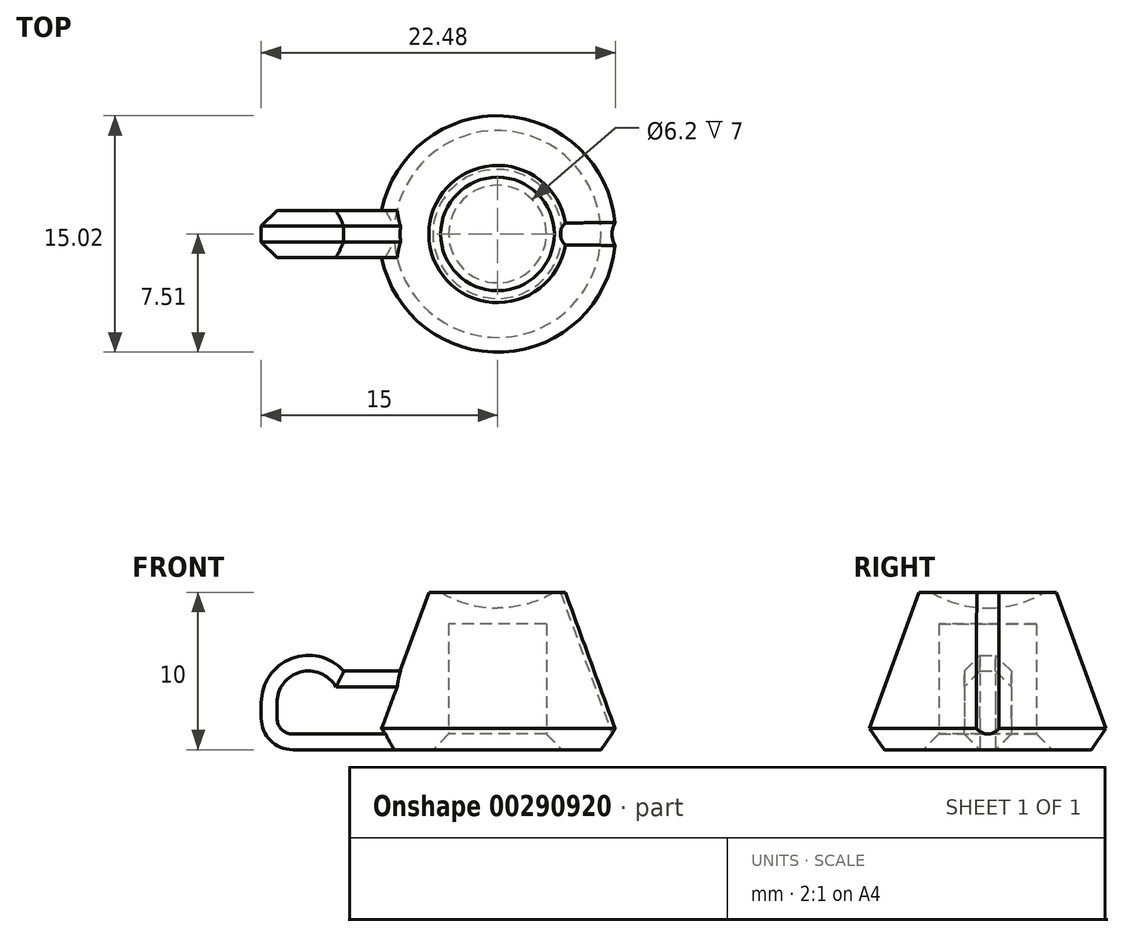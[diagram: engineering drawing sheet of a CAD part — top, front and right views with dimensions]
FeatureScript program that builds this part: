
annotation { "Feature Type Name" : "Feature", "Feature Type Description" : "" }
export const myFeature = defineFeature(function(context is Context, id is Id, definition is map)
    precondition{}
    {
        {
            var Q0;
            Q0=qCreatedBy(makeId("Top.planeOp"),FACE);
            var sketch = newSketch(context, id + "F0", { "sketchPlane" : qUnion([Q0])});
            skCircle(sketch, "E0", {"center": v(0, 0) * mm, "radius": 3.1 * mm});
            skCircle(sketch, "E1", {"center": v(0, 0) * mm, "radius": 13 * mm, "construction": true});
            skCircle(sketch, "E2", {"center": v(0, 0) * mm, "radius": 8 * mm});
            skSolve(sketch);
        }
        {
            var Q0;
            Q0=makeQuery(id+"F0.imprint","IMPRINT",FACE,{"disambiguationData":[TD([[makeQuery(id+"F0.imprint","IMPRINT",EDGE,{"derivedFrom":sQuery(id+"F0.wireOp",EDGE,"E0")}),-1.0]])]});
            var Q1;
            Q1=makeQuery(id+"F0.imprint","IMPRINT",FACE,{"disambiguationData":[TD([[makeQuery(id+"F0.imprint","IMPRINT",EDGE,{"derivedFrom":sQuery(id+"F0.wireOp",EDGE,"E0")}),1.0]])]});
            extrude(context, id + "F1", {"entities" : qUnion([Q0, Q1]), "depth" : 10 * mm, "hasDraft" : true, "draftAngle" : 20 * degree, "draftPullDirection" : true});
        }
        {
            var Q0;
            Q0=qCreatedBy(makeId("Front.planeOp"),FACE);
            var sketch = newSketch(context, id + "F2", { "sketchPlane" : qUnion([Q0])});
            skCircle(sketch, "E3", {"center": v(-12, 3) * mm, "radius": 3 * mm});
            skLineSegment(sketch, "E4", {"start": v(-15, 15.23) * mm, "end": v(-15, 2) * mm, "construction": true});
            skLineSegment(sketch, "E5", {"start": v(-15, 6) * mm, "end": v(-4.6, 6) * mm, "construction": true});
            skLineSegment(sketch, "E6", {"start": v(0, 0) * mm, "end": v(-12, 0) * mm});
            skLineSegment(sketch, "E7", {"start": v(0, 0) * mm, "end": v(0, 5) * mm});
            skLineSegment(sketch, "E8", {"start": v(0, 5) * mm, "end": v(-9.76, 5) * mm});
            skLineSegment(sketch, "E9", {"start": v(-12, 0) * mm, "end": v(-13, 0) * mm});
            skLineSegment(sketch, "E10", {"start": v(-15, -2) * mm, "end": v(-15, 3) * mm});
            skArc(sketch, "E11.filletArc", {"start": v(-15, 2) * mm, "mid": v(-14.41, 0.59) * mm, "end": v(-13, 0) * mm});
            skSolve(sketch);
        }
        {
            var Q0;
            Q0=makeQuery(id+"F2.imprint","IMPRINT",FACE,{"disambiguationData":[TD([[makeQuery(id+"F2.imprint","IMPRINT",EDGE,{"derivedFrom":sQuery(id+"F2.wireOp",EDGE,"E3")}),1.0]])]});
            var Q1;
            {var subQ0=sQuery(id+"F2.wireOp",EDGE,"E9");Q1=makeQuery(id+"F2.imprint","IMPRINT",FACE,{"disambiguationData":[TD([[makeQuery(id+"F2.imprint","IMPRINT",EDGE,{"derivedFrom":subQ0}),-1.0]])]});}
            var Q2;
            {var subQ0=sQuery(id+"F2.wireOp",EDGE,"E6");Q2=makeQuery(id+"F2.imprint","IMPRINT",FACE,{"disambiguationData":[TD([[makeQuery(id+"F2.imprint","IMPRINT",EDGE,{"derivedFrom":subQ0}),-1.0]])]});}
            extrude(context, id + "F3", {"entities" : qUnion([Q0, Q1, Q2]), "operationType" : NewBodyOperationType.ADD, "depth" : 1.5 * mm, "hasSecondDirection" : true, "secondDirectionOppositeDirection" : true, "secondDirectionDepth" : 1.5 * mm});
        }
        {
            var Q0;
            Q0=makeQuery(id+"F0.imprint","IMPRINT",FACE,{"disambiguationData":[TD([[makeQuery(id+"F0.imprint","IMPRINT",EDGE,{"derivedFrom":sQuery(id+"F0.wireOp",EDGE,"E0")}),1.0]])]});
            extrude(context, id + "F4", {"entities" : qUnion([Q0]), "operationType" : NewBodyOperationType.REMOVE, "depth" : 8 * mm});
        }
        {
            var Q0;
            Q0=qCreatedBy(makeId("Front.planeOp"),FACE);
            var sketch = newSketch(context, id + "F5", { "sketchPlane" : qUnion([Q0])});
            skCircle(sketch, "E12", {"center": v(0, 16) * mm, "radius": 7 * mm});
            skLineSegment(sketch, "E13", {"start": v(0, 24.17) * mm, "end": v(0, 0) * mm, "construction": true});
            skLineSegment(sketch, "E14", {"start": v(0, 23) * mm, "end": v(0, 9) * mm});
            skSolve(sketch);
        }
        {
            var Q0;
            {var subQ0=sQuery(id+"F5.wireOp",EDGE,"E14");Q0=makeQuery(id+"F5.imprint","IMPRINT",FACE,{"disambiguationData":[TD([[makeQuery(id+"F5.imprint","IMPRINT",EDGE,{"derivedFrom":subQ0}),-1.0]])]});}
            var Q1;
            Q1=sQuery(id+"F5.wireOp",EDGE,"E14");
            revolve(context, id + "F6", {"operationType" : NewBodyOperationType.REMOVE, "entities" : qUnion([Q0]), "axis" : qUnion([Q1]), "revolveType" : RevolveType.FULL, "oppositeDirection" : true});
        }
        {
            var Q0;
            Q0=makeQuery(id+"F3.boolean.opBoolean","MERGE",FACE,{"derivedFrom":[makeQuery(id+"F1.opExtrude","CAP_FACE",FACE,{"disambiguationData":[OSD([sQuery(id+"F0.wireOp",EDGE,"E2")])],"isStart":true}),makeQuery(id+"F3.opExtrude","SWEPT_FACE",FACE,{"disambiguationData":[OSD([sQuery(id+"F2.wireOp",EDGE,"E6"),sQuery(id+"F2.wireOp",EDGE,"E9")])]})]});
            var Q1;
            Q1=makeQuery(id+"F3.opExtrude","CAP_EDGE",EDGE,{"disambiguationData":[OSD([sQuery(id+"F2.wireOp",EDGE,"E8")])],"isStart":false});
            var Q2;
            Q2=makeQuery(id+"F3.opExtrude","CAP_EDGE",EDGE,{"disambiguationData":[OSD([sQuery(id+"F2.wireOp",EDGE,"E8")])],"isStart":true});
            chamfer(context, id + "F7", {"entities" : qUnion([Q0, Q1, Q2]), "width" : 1 * mm, "tangentPropagation" : true});
        }
        {
            var Q0;
            Q0=qCreatedBy(makeId("Front.planeOp"),FACE);
            var sketch = newSketch(context, id + "F8", { "sketchPlane" : qUnion([Q0])});
            skLineSegment(sketch, "E15", {"start": v(3.34, 14.74) * mm, "end": v(9.34, -1.75) * mm, "construction": true});
            skLineSegment(sketch, "E16", {"start": v(4.7, 11.02) * mm, "end": v(3.75, 10.68) * mm});
            skLineSegment(sketch, "E17", {"start": v(3.75, 10.68) * mm, "end": v(7.55, 0.25) * mm});
            skLineSegment(sketch, "E18", {"start": v(7.55, 0.25) * mm, "end": v(8.49, 0.59) * mm});
            skLineSegment(sketch, "E19", {"start": v(4.7, 11.02) * mm, "end": v(8.49, 0.59) * mm});
            skSolve(sketch);
        }
        {
            var Q0;
            Q0=makeQuery(id+"F8.imprint","IMPRINT",FACE,{"disambiguationData":[TD([[makeQuery(id+"F8.imprint","IMPRINT",EDGE,{"derivedFrom":sQuery(id+"F8.wireOp",EDGE,"E16")}),1.0]])]});
            var Q1;
            Q1=sQuery(id+"F8.wireOp",EDGE,"E19");
            revolve(context, id + "F9", {"operationType" : NewBodyOperationType.REMOVE, "entities" : qUnion([Q0]), "axis" : qUnion([Q1]), "revolveType" : RevolveType.FULL, "oppositeDirection" : true});
        }
    });
